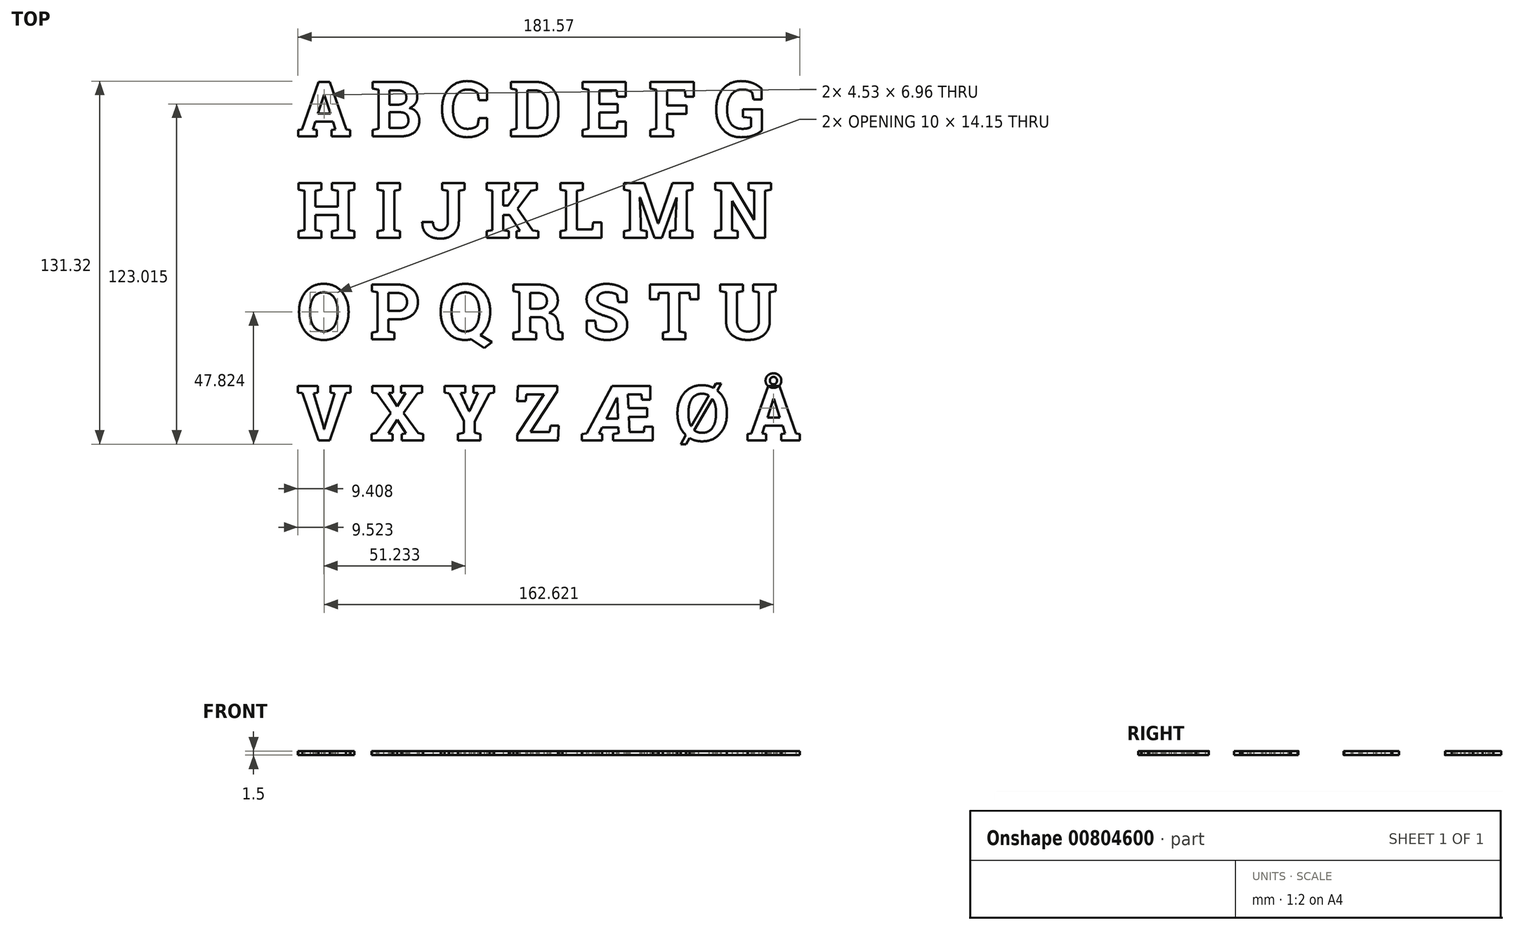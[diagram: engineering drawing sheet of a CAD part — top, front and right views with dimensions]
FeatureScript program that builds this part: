
annotation { "Feature Type Name" : "Feature", "Feature Type Description" : "" }
export const myFeature = defineFeature(function(context is Context, id is Id, definition is map)
    precondition{}
    {
        {
            var Q0;
            Q0=qCreatedBy(makeId("Top.planeOp"),FACE);
            var sketch = newSketch(context, id + "F0", { "sketchPlane" : qUnion([Q0])});
            skText(sketch, "E0", { "text": "A B C D E F G \nH I J K L M N\nO P Q R S T U \nV X Y Z Æ Ø Å", "fontName": "RobotoSlab-Bold.ttf"});
            const initialGuessF0  = {"E0": [-0.09187, -0.02, 1, 0, 0.02]};
            skSetInitialGuess(sketch, initialGuessF0);
            skSolve(sketch);
        }
        {
            var Q0;
            Q0 = qSketchRegion(id + "F0", true);
            extrude(context, id + "F1", {"entities" : qUnion([Q0]), "depth" : 1.5 * mm, "offsetDistance" : 25 * mm});
        }
        {
            var Q0;
            Q0=makeQuery(id+"F1.opExtrude","SWEPT_BODY",BODY,{"disambiguationData":[OSD([sQuery(id+"F0.wireOp",EDGE,"E0.sketch_text.stroke-664"),sQuery(id+"F0.wireOp",EDGE,"E0.sketch_text.stroke-665"),sQuery(id+"F0.wireOp",EDGE,"E0.sketch_text.stroke-666"),sQuery(id+"F0.wireOp",EDGE,"E0.sketch_text.stroke-667"),sQuery(id+"F0.wireOp",EDGE,"E0.sketch_text.stroke-668"),sQuery(id+"F0.wireOp",EDGE,"E0.sketch_text.stroke-669"),sQuery(id+"F0.wireOp",EDGE,"E0.sketch_text.stroke-670"),sQuery(id+"F0.wireOp",EDGE,"E0.sketch_text.stroke-671"),sQuery(id+"F0.wireOp",EDGE,"E0.sketch_text.stroke-672"),sQuery(id+"F0.wireOp",EDGE,"E0.sketch_text.stroke-673"),sQuery(id+"F0.wireOp",EDGE,"E0.sketch_text.stroke-674"),sQuery(id+"F0.wireOp",EDGE,"E0.sketch_text.stroke-675"),sQuery(id+"F0.wireOp",EDGE,"E0.sketch_text.stroke-676"),sQuery(id+"F0.wireOp",EDGE,"E0.sketch_text.stroke-677"),sQuery(id+"F0.wireOp",EDGE,"E0.sketch_text.stroke-678"),sQuery(id+"F0.wireOp",EDGE,"E0.sketch_text.stroke-679")])]});
            transform(context, id + "F2", {"entities" : qUnion([Q0]), "transformType" : TransformType.TRANSLATION_3D, "dx" : 0 * mm, "dy" : -2 * mm, "dz" : 0 * mm, "makeCopy" : false});
        }
    });
